# Revit family: Haworth_Immerse_SingleTable_RectangleTwoPieceTop
name_source: partatom
category: Furniture Systems
revit_build: Autodesk Revit 2018 (Build: 20170223_1515(x64)
units: mm (PartAtom-declared; Revit-internal decimal feet)

## family parameters
Always vertical = Yes
Cut with Voids When Loaded = No
OmniClass Number = 23.40.70.14.64.21
OmniClass Title = Systems Furniture
Part Type = Normal
Room Calculation Point = No
Round Connector Dimension = Use Diameter
Shared = No
Work Plane-Based = No

## types (4) — shared parameters
Actual Height = 29"
Actual Width = 144"
Assembly Code = E2020200
Lower Top Cutout Depth = 12 1/2"
Lower Top Cutout Width = 78"
Lower Top Thickness = 1/8"
Lower Top Width = 142"
Manufacturer = Haworth
Model = THRA-60E4
Revision Number = 1
Size = Verify Final Dim. w/ Haworth
Standard Depths = 48, 60 in.
Standard Heights = 29 in.
Standard Widths = 144 in.
URL = https://www.haworth.com
URL - Product = http://www.haworth.com
Understructure Overall Width = 81"
Understucture Thickness = 3 1/2"
Upper Top Thickness = 1 3/16"
Warranty = http://www.haworth.com

## per-type parameters (varying)
| type | Actual Depth | Description | Oblong Planter | Oblong Planter Void Height | Understructure Depth |
| 48d 144w 29h - Oblong Planter | 48" | Haworth Immerse Single Table Rectangle Two Piece Top - 48d 144w 29h - Oblong Planter | Yes | 2" | 16" |
| 48d 144w 29h - No Planter | 48" | Haworth Immerse Single Table Rectangle Two Piece Top - 48d 144w 29h - No Planter | No | 13/128" | 16" |
| 60d 144w 29h - Oblong Planter | 60" | Haworth Immerse Single Table Rectangle Two Piece Top - 60d 144w 29h - Oblong Planter | Yes | 2" | 20" |
| 60d 144w 29h - No Planter | 60" | Haworth Immerse Single Table Rectangle Two Piece Top - 60d 144w 29h - No Planter | No | 13/128" | 20" |

## geometry (parser evidence)
native form markers: Sweep x5
no freeform markers — native parametric forms only
